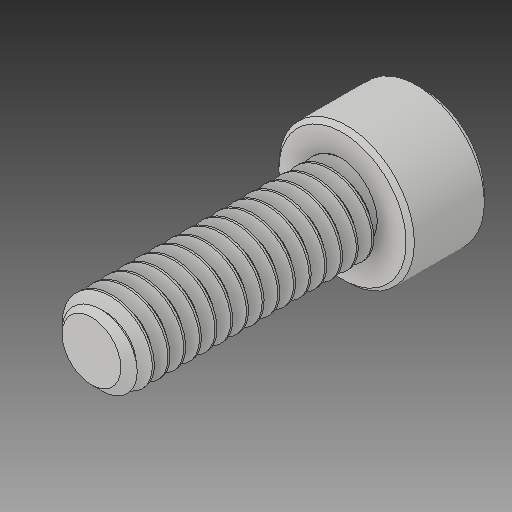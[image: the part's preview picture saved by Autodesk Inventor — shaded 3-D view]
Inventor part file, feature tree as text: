
AUTODESK INVENTOR PART (.ipt)
format: ipt  version: 2017 (Build 210142000, 142)  size: 683,008 bytes
history: native  units: in
note: dims shown in document units (in); Inventor stores cm internally (conversion verified against a paired STEP export)
features: chamfer x1
ambient origin geometry x8: Origin, YZ Plane, XZ Plane, XY Plane, X Axis, Y Axis, Z Axis, Center Point
bodies: Solid1 (feature_tree)
feature tree (1):
  chamfer  "Chamfer2"  [1 undecoded]
note: 1 required parameter value undecoded (feature->parameter linkage not recoverable at this tier; creation-order binding heuristic only, values carry confidence <= 0.55)
